# Revit family: Scout Chandelier
name_source: partatom
category: Lighting Fixtures
revit_build: Autodesk Revit 2017 (Build: 20190508_0315(x64)
units: mm (PartAtom-declared; Revit-internal decimal feet)

## family parameters
Cut with Voids When Loaded = No
Host = Face
Light Source = Yes
Part Type = Normal
Room Calculation Point = No
Round Connector Dimension = Use Diameter
Shared = No

## types (1)
- Scout Chandelier
    Canopy Width = 6"
    Color Filter = 16777215
    Cost = 519 $
    Default Elevation = 0"
    Description = Crafted from heavy-gauge solid brass, the Scout Chandelier is a nod to the factory movement of the early 20th century. A celebration of American manufacturing, its striking silhouette pairs the durability of industrial lighting with a modern aesthetic. Assembled in our Portland, Ore. factory using ethically-sourced domestic and global components. A Schoolhouse Original.
    Dimming Lamp Color Temperature Shift = <None>
    Height = 15"
    Light Source Symbol Length = 5"
    Max Wattage = 100 W
    Primary Finishes = Satin Nickel, True Black, Natural Brass
    Product Material = Schoolhouse_Brass
    Spot Beam Angle = 30.00°
    Spot Field Angle = 90.00°
    Tilt Angle = 60.00°
    URL = https://www.schoolhouse.com
    Voltage = 120 /220V
    Width = 16 1/2"

## geometry (parser evidence)
native form markers: Sweep x3
no freeform markers — native parametric forms only
